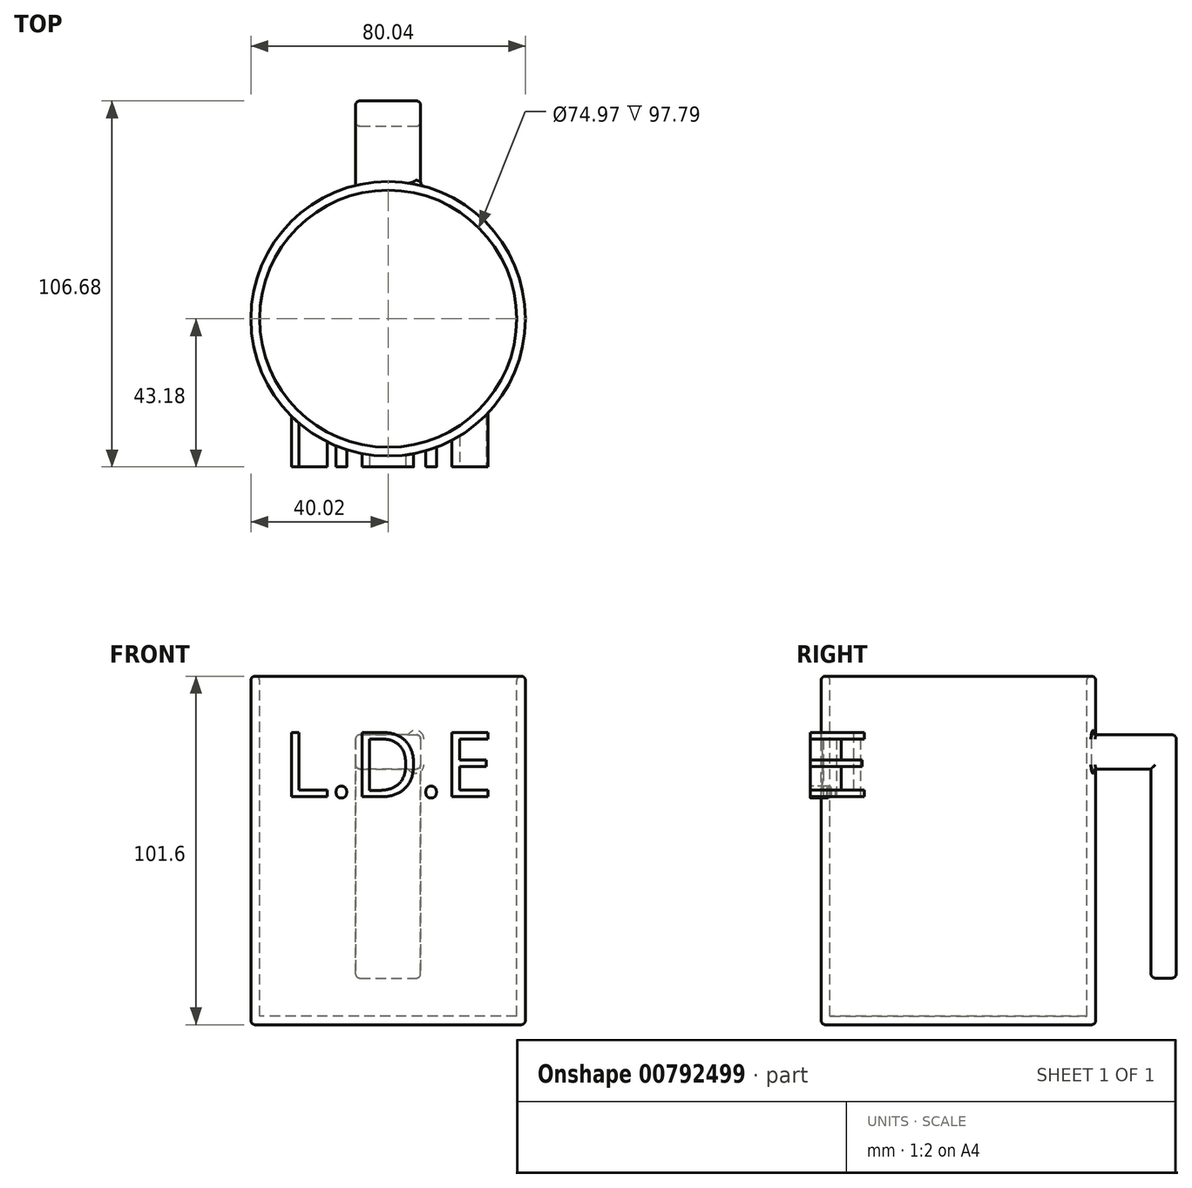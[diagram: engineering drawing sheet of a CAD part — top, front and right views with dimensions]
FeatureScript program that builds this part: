
annotation { "Feature Type Name" : "Feature", "Feature Type Description" : "" }
export const myFeature = defineFeature(function(context is Context, id is Id, definition is map)
    precondition{}
    {
        {
            var Q0;
            Q0=qCreatedBy(makeId("Top.planeOp"),FACE);
            cPlane(context, id + "F0", {"entities" : qUnion([Q0]), "cplaneType" : CPlaneType.OFFSET, "offset" : 43.18 * mm, "width" : 152.4 * mm, "height" : 152.4 * mm});
        }
        {
            var Q0;
            Q0=qCreatedBy(id+"F0.planeOp",FACE);
            var sketch = newSketch(context, id + "F1", { "sketchPlane" : qUnion([Q0])});
            skCircle(sketch, "E0", {"center": v(0, 0) * mm, "radius": 40.02 * mm});
            skSolve(sketch);
        }
        {
            var Q0;
            Q0=makeQuery(id+"F1.imprint","IMPRINT",FACE,{"disambiguationData":[TD([[makeQuery(id+"F1.imprint","IMPRINT",EDGE,{"derivedFrom":sQuery(id+"F1.wireOp",EDGE,"E0")}),1.0]])]});
            extrude(context, id + "F2", {"entities" : qUnion([Q0]), "oppositeDirection" : true, "depth" : 101.6 * mm, "offsetDistance" : 25.4 * mm});
        }
        {
            var Q0;
            Q0=makeQuery(id+"F2.opExtrude","CAP_FACE",FACE,{"disambiguationData":[OSD([sQuery(id+"F1.wireOp",EDGE,"E0")])],"isStart":true});
            shell(context, id + "F3", {"entities" : qUnion([Q0]), "thickness" : 2.54 * mm});
        }
        {
            var Q0;
            {var subQ0=sQuery(id+"F1.wireOp",EDGE,"E0");Q0=makeQuery(id+"F3.opShell","OFFSET_EDGE",EDGE,{"disambiguationData":[OSD([subQ0]),TDD([makeQuery(id+"F2.opExtrude","CAP_EDGE",EDGE,{"disambiguationData":[OSD([subQ0])],"isStart":true})])]});}
            var Q1;
            Q1=makeQuery(id+"F2.opExtrude","CAP_EDGE",EDGE,{"disambiguationData":[OSD([sQuery(id+"F1.wireOp",EDGE,"E0")])],"isStart":true});
            var Q2;
            Q2=makeQuery(id+"F2.opExtrude","CAP_EDGE",EDGE,{"disambiguationData":[OSD([sQuery(id+"F1.wireOp",EDGE,"E0")])],"isStart":false});
            fillet(context, id + "F4", {"entities" : qUnion([Q0, Q1, Q2]), "radius" : 1.27 * mm, "tangentPropagation" : true, "allowEdgeOverflow" : false});
        }
        {
            var Q0;
            Q0=qCreatedBy(makeId("Front.planeOp"),FACE);
            cPlane(context, id + "F5", {"entities" : qUnion([Q0]), "cplaneType" : CPlaneType.OFFSET, "offset" : 63.5 * mm, "oppositeDirection" : true, "width" : 152.4 * mm, "height" : 152.4 * mm});
        }
        {
            var Q0;
            Q0=qCreatedBy(id+"F5.planeOp",FACE);
            var sketch = newSketch(context, id + "F6", { "sketchPlane" : qUnion([Q0])});
            skLineSegment(sketch, "E1.bottom", {"start": v(0, 26.09) * mm, "end": v(-9.5, 26.09) * mm});
            skLineSegment(sketch, "E1.top", {"start": v(0, 16.13) * mm, "end": v(-9.5, 16.13) * mm});
            skLineSegment(sketch, "E1.left", {"start": v(0, 26.09) * mm, "end": v(0, 16.13) * mm});
            skLineSegment(sketch, "E1.right", {"start": v(-9.5, 26.09) * mm, "end": v(-9.5, 16.13) * mm});
            skLineSegment(sketch, "E2.MirrorCS", {"start": v(0, 26.09) * mm, "end": v(9.5, 26.09) * mm});
            skLineSegment(sketch, "E3.MirrorCS", {"start": v(0, 16.13) * mm, "end": v(9.5, 16.13) * mm});
            skLineSegment(sketch, "E4.MirrorCS", {"start": v(9.5, 26.09) * mm, "end": v(9.5, 16.13) * mm});
            skSolve(sketch);
        }
        {
            var Q0;
            Q0=makeQuery(id+"F6.imprint","IMPRINT",FACE,{"disambiguationData":[TD([[makeQuery(id+"F6.imprint","IMPRINT",EDGE,{"derivedFrom":sQuery(id+"F6.wireOp",EDGE,"E1.left")}),1.0]])]});
            var Q1;
            Q1=makeQuery(id+"F6.imprint","IMPRINT",FACE,{"disambiguationData":[TD([[makeQuery(id+"F6.imprint","IMPRINT",EDGE,{"derivedFrom":sQuery(id+"F6.wireOp",EDGE,"E1.bottom")}),1.0]])]});
            extrude(context, id + "F7", {"entities" : qUnion([Q0, Q1]), "operationType" : NewBodyOperationType.ADD, "depth" : 25.4 * mm, "offsetDistance" : 25.4 * mm});
        }
        {
            var Q0;
            Q0=makeQuery(id+"F7.opExtrude","SWEPT_FACE",FACE,{"disambiguationData":[OSD([sQuery(id+"F6.wireOp",EDGE,"E1.top"),sQuery(id+"F6.wireOp",EDGE,"E3.MirrorCS")])]});
            var sketch = newSketch(context, id + "F8", { "sketchPlane" : qUnion([Q0])});
            skLineSegment(sketch, "E5.bottom", {"start": v(-9.5, -63.5) * mm, "end": v(9.5, -63.5) * mm});
            skLineSegment(sketch, "E5.top", {"start": v(-9.5, -56.16) * mm, "end": v(9.5, -56.16) * mm});
            skLineSegment(sketch, "E5.left", {"start": v(-9.5, -63.5) * mm, "end": v(-9.5, -56.16) * mm});
            skLineSegment(sketch, "E5.right", {"start": v(9.5, -63.5) * mm, "end": v(9.5, -56.16) * mm});
            skSolve(sketch);
        }
        {
            var Q0;
            Q0=makeQuery(id+"F8.imprint","IMPRINT",FACE,{"disambiguationData":[TD([[makeQuery(id+"F8.imprint","IMPRINT",EDGE,{"derivedFrom":sQuery(id+"F8.wireOp",EDGE,"E5.bottom")}),1.0]])]});
            extrude(context, id + "F9", {"entities" : qUnion([Q0]), "operationType" : NewBodyOperationType.ADD, "depth" : 60.96 * mm, "offsetDistance" : 25.4 * mm});
        }
        {
            var Q0;
            Q0=makeQuery(id+"F7.opExtrude","CAP_EDGE",EDGE,{"disambiguationData":[OSD([sQuery(id+"F6.wireOp",EDGE,"E1.bottom"),sQuery(id+"F6.wireOp",EDGE,"E2.MirrorCS")])],"isStart":true});
            var Q1;
            Q1=makeQuery(id+"F7.opExtrude","SWEPT_EDGE",EDGE,{"disambiguationData":[OSD([sQuery(id+"F6.wireOp",EDGE,"E2.MirrorCS"),sQuery(id+"F6.wireOp",EDGE,"E4.MirrorCS")])]});
            var Q2;
            Q2=makeQuery(id+"F9.boolean.opBoolean","MERGE",FACE,{"derivedFrom":[makeQuery(id+"F7.opExtrude","SWEPT_FACE",FACE,{"disambiguationData":[OSD([sQuery(id+"F6.wireOp",EDGE,"E4.MirrorCS")])]}),makeQuery(id+"F9.opExtrude","SWEPT_FACE",FACE,{"disambiguationData":[OSD([sQuery(id+"F8.wireOp",EDGE,"E5.right")])]})]});
            var Q3;
            Q3=makeQuery(id+"F9.boolean.opBoolean","MERGE",EDGE,{"derivedFrom":[makeQuery(id+"F7.opExtrude","CAP_EDGE",EDGE,{"disambiguationData":[OSD([sQuery(id+"F6.wireOp",EDGE,"E4.MirrorCS")])],"isStart":true}),makeQuery(id+"F9.opExtrude","SWEPT_EDGE",EDGE,{"disambiguationData":[OSD([sQuery(id+"F8.wireOp",EDGE,"E5.bottom"),sQuery(id+"F8.wireOp",EDGE,"E5.right")])]})]});
            var Q4;
            Q4=makeQuery(id+"F9.boolean.opBoolean","MERGE",EDGE,{"derivedFrom":[makeQuery(id+"F7.opExtrude","CAP_EDGE",EDGE,{"disambiguationData":[OSD([sQuery(id+"F6.wireOp",EDGE,"E1.right")])],"isStart":true}),makeQuery(id+"F9.opExtrude","SWEPT_EDGE",EDGE,{"disambiguationData":[OSD([sQuery(id+"F8.wireOp",EDGE,"E5.bottom"),sQuery(id+"F8.wireOp",EDGE,"E5.left")])]})]});
            var Q5;
            Q5=makeQuery(id+"F7.opExtrude","SWEPT_EDGE",EDGE,{"disambiguationData":[OSD([sQuery(id+"F6.wireOp",EDGE,"E1.top"),sQuery(id+"F6.wireOp",EDGE,"E1.right")])]});
            var Q6;
            Q6=makeQuery(id+"F9.opExtrude","SWEPT_EDGE",EDGE,{"disambiguationData":[OSD([sQuery(id+"F6.wireOp",EDGE,"E1.top"),sQuery(id+"F6.wireOp",EDGE,"E1.right"),sQuery(id+"F8.wireOp",EDGE,"E5.top"),sQuery(id+"F8.wireOp",EDGE,"E5.left")])]});
            var Q7;
            Q7=makeQuery(id+"F7.opExtrude","SWEPT_EDGE",EDGE,{"disambiguationData":[OSD([sQuery(id+"F6.wireOp",EDGE,"E1.bottom"),sQuery(id+"F6.wireOp",EDGE,"E1.right")])]});
            var Q8;
            Q8=makeQuery(id+"F7.opExtrude","SWEPT_EDGE",EDGE,{"disambiguationData":[OSD([sQuery(id+"F6.wireOp",EDGE,"E3.MirrorCS"),sQuery(id+"F6.wireOp",EDGE,"E4.MirrorCS")])]});
            var Q9;
            Q9=makeQuery(id+"F9.opExtrude","CAP_EDGE",EDGE,{"disambiguationData":[OSD([sQuery(id+"F8.wireOp",EDGE,"E5.bottom")])],"isStart":false});
            var Q10;
            Q10=makeQuery(id+"F9.opExtrude","CAP_EDGE",EDGE,{"disambiguationData":[OSD([sQuery(id+"F8.wireOp",EDGE,"E5.top")])],"isStart":false});
            var Q11;
            Q11=makeQuery(id+"F9.opExtrude","CAP_EDGE",EDGE,{"disambiguationData":[OSD([sQuery(id+"F8.wireOp",EDGE,"E5.left")])],"isStart":false});
            fillet(context, id + "F10", {"entities" : qUnion([Q0, Q1, Q2, Q3, Q4, Q5, Q6, Q7, Q8, Q9, Q10, Q11]), "radius" : 1.27 * mm, "tangentPropagation" : true, "allowEdgeOverflow" : false});
        }
        {
            var Q0;
            Q0=qCreatedBy(makeId("Front.planeOp"),FACE);
            cPlane(context, id + "F11", {"entities" : qUnion([Q0]), "cplaneType" : CPlaneType.OFFSET, "offset" : 43.18 * mm, "width" : 152.4 * mm, "height" : 152.4 * mm});
        }
        {
            var Q0;
            Q0=qCreatedBy(id+"F11.planeOp",FACE);
            var sketch = newSketch(context, id + "F12", { "sketchPlane" : qUnion([Q0])});
            skText(sketch, "E6", { "text": "L.D.E", "fontName": "OpenSans-Regular.ttf"});
            const initialGuessF12  = {"E6": [-0.03077, 0.00802, 1, 0, 0.01893]};
            skSetInitialGuess(sketch, initialGuessF12);
            skSolve(sketch);
        }
        {
            var Q0;
            Q0 = qSketchRegion(id + "F12", true);
            extrude(context, id + "F13", {"entities" : qUnion([Q0]), "endBound" : BoundingType.UP_TO_NEXT, "oppositeDirection" : true, "depth" : 25.4 * mm, "offsetDistance" : 25.4 * mm});
        }
    });
